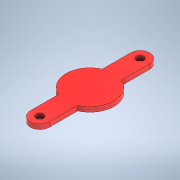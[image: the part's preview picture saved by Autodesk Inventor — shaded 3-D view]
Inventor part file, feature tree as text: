
AUTODESK INVENTOR PART (.ipt)
format: ipt  version: 2021 (Build 250183000, 183)  size: 121,344 bytes
history: native  units: mm
features: other x1, extrude x1, sketch x1
ambient origin geometry x8: Origin, YZ Plane, XZ Plane, XY Plane, X Axis, Y Axis, Z Axis, Center Point
bodies: Solid1 (feature_tree)
feature tree (3):
  other  "<userpath>\Documents\Semestre8\Robótica\Proyecto-Rob\Piezas\ParámetrosGripper.xlsx"
  extrude  "Extrusion1"  Depth=5.0mm
  sketch  "Sketch1"  dims[d0=50.0mm d1=8.0mm d2=8.0mm d3=20.0mm d4=105.0mm d5=5.0mm d6=0.0mm]
